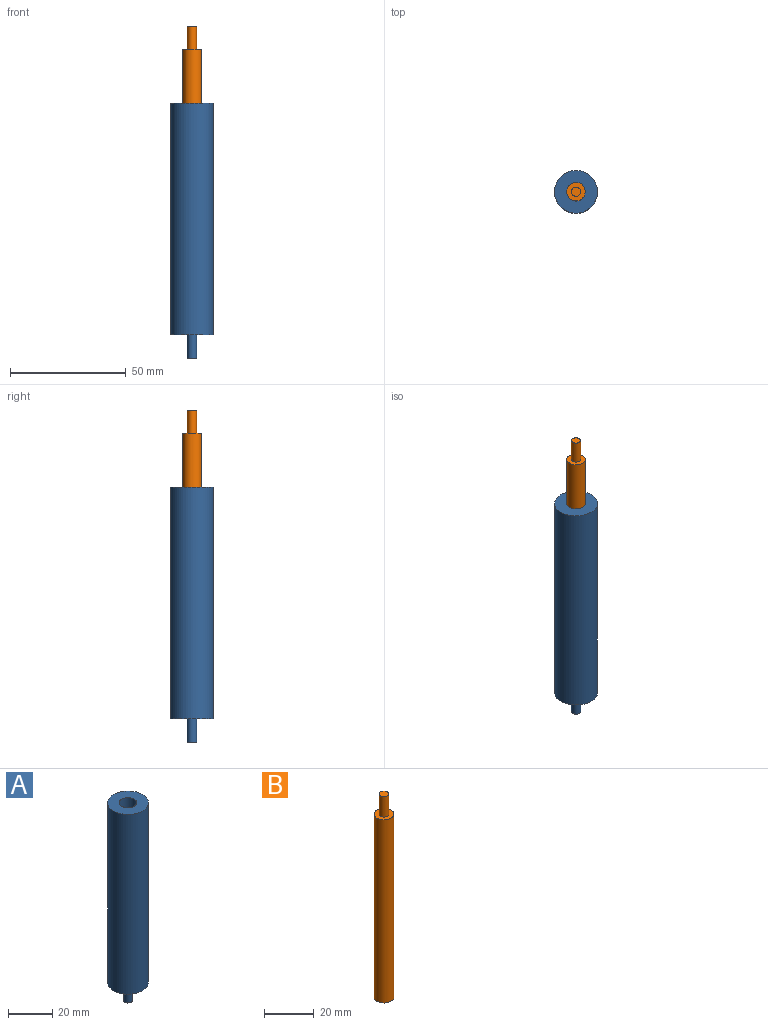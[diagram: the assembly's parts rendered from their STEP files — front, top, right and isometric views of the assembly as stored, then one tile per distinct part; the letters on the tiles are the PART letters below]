
ASSEMBLY  parts=2 mates=1
PART A: 7 faces, bbox 18.5x18.5x110 mm
  f0: cylinder r=9.25mm len=100mm, axis (0,0,-1), area 5811.9mm2, adj f1,f2
  f1: plane 18.5x18.5mm, normal (0,0,1), area 218.5mm2, adj f0,f3
  f2: plane 18.5x18.5mm, normal (0,0,-1), area 256.2mm2, adj f0,f5
  f3: cylinder r=4mm len=90mm, axis (0,0,1), area 2261.9mm2, adj f1,f4
  f4: plane 8x8mm, normal (0,0,1), area 50.3mm2, adj f3
  f5: cylinder r=2mm len=10mm, axis (0,0,1), area 125.7mm2, adj f2,f6
  f6: plane 4x4mm, normal (0,0,-1), area 12.6mm2, adj f5
PART B: 5 faces, bbox 8x8x100 mm
  f0: cylinder r=4mm len=90mm, axis (0,0,-1), area 2261.9mm2, adj f1,f2
  f1: plane 8x8mm, normal (0,0,1), area 37.7mm2, adj f0,f3
  f2: plane 8x8mm, normal (0,0,-1), area 50.3mm2, adj f0
  f3: cylinder r=2mm len=10mm, axis (0,0,-1), area 125.7mm2, adj f1,f4
  f4: plane 4x4mm, normal (0,0,1), area 12.6mm2, adj f3
PLACE A at identity fixed
PLACE B t=(0,0,33.29)mm
MATE slider B.f0 <-> A.f0  axis (0,0,-1) through (0,0,78.29)mm
